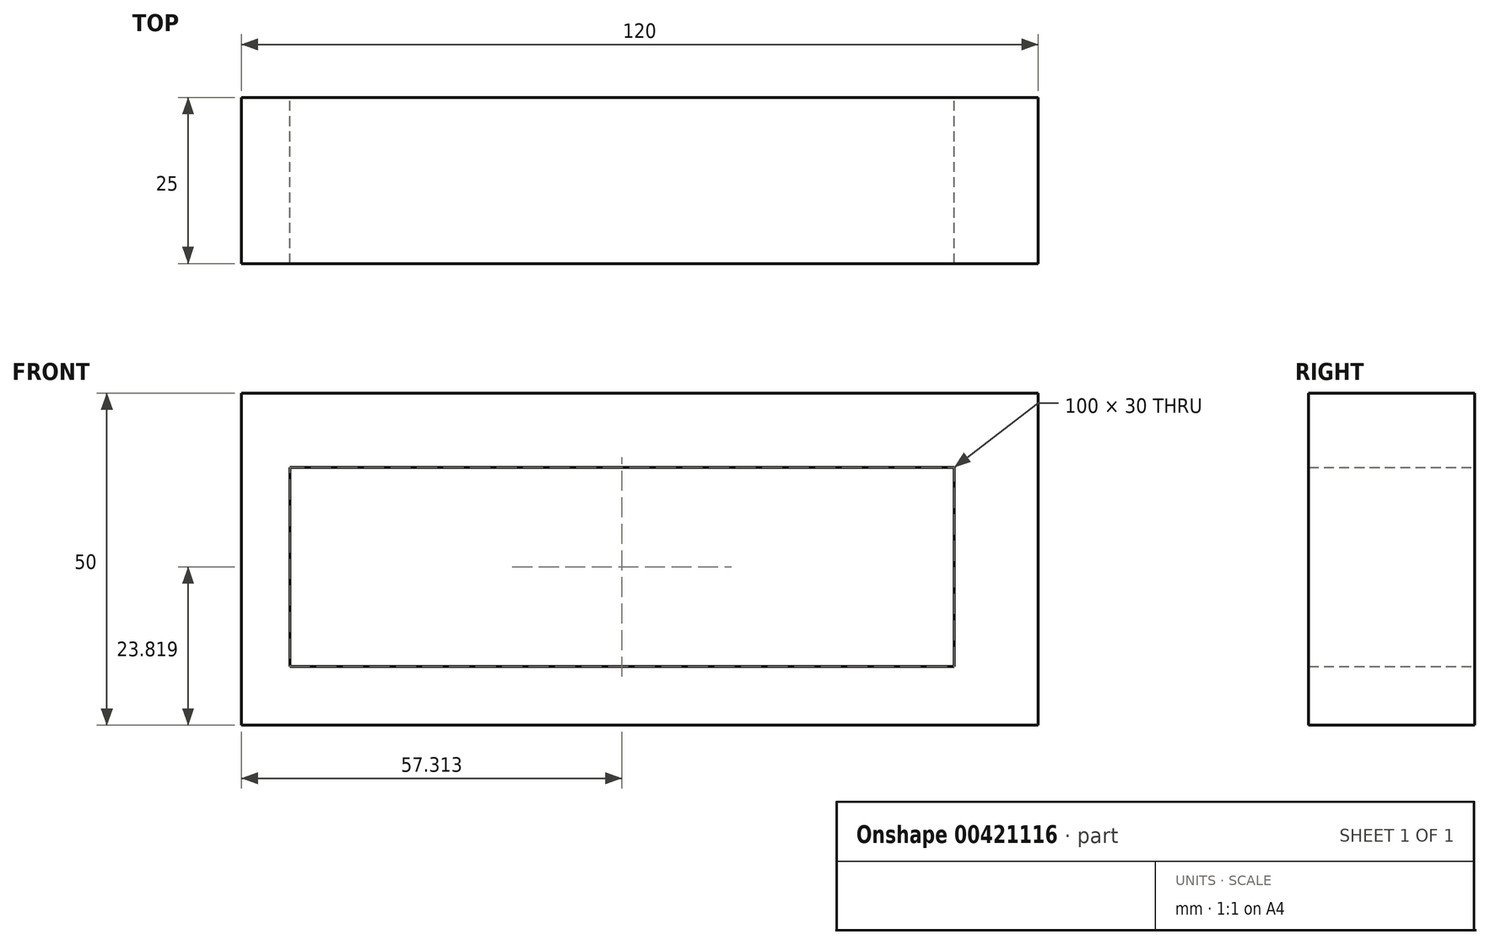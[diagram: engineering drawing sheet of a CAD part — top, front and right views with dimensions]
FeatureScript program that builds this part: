
annotation { "Feature Type Name" : "Feature", "Feature Type Description" : "" }
export const myFeature = defineFeature(function(context is Context, id is Id, definition is map)
    precondition{}
    {
        {
            var Q0;
            Q0=qCreatedBy(makeId("Front.planeOp"),FACE);
            var sketch = newSketch(context, id + "F0", { "sketchPlane" : qUnion([Q0])});
            skLineSegment(sketch, "E0.bottom", {"start": v(-120, 50) * mm, "end": v(0, 50) * mm});
            skLineSegment(sketch, "E0.top", {"start": v(-120, 0) * mm, "end": v(0, 0) * mm});
            skLineSegment(sketch, "E0.left", {"start": v(-120, 50) * mm, "end": v(-120, 0) * mm});
            skLineSegment(sketch, "E0.right", {"start": v(0, 50) * mm, "end": v(0, 0) * mm});
            skLineSegment(sketch, "E1.bottom", {"start": v(-112.69, 38.82) * mm, "end": v(-12.69, 38.82) * mm});
            skLineSegment(sketch, "E1.top", {"start": v(-112.69, 8.82) * mm, "end": v(-12.69, 8.82) * mm});
            skLineSegment(sketch, "E1.left", {"start": v(-112.69, 38.82) * mm, "end": v(-112.69, 8.82) * mm});
            skLineSegment(sketch, "E1.right", {"start": v(-12.69, 38.82) * mm, "end": v(-12.69, 8.82) * mm});
            skSolve(sketch);
        }
        {
            var Q0;
            Q0=makeQuery(id+"F0.imprint","IMPRINT",FACE,{"disambiguationData":[TD([[makeQuery(id+"F0.imprint","IMPRINT",EDGE,{"derivedFrom":sQuery(id+"F0.wireOp",EDGE,"E0.bottom")}),-1.0]])]});
            extrude(context, id + "F1", {"entities" : qUnion([Q0]), "depth" : 25 * mm});
        }
    });
